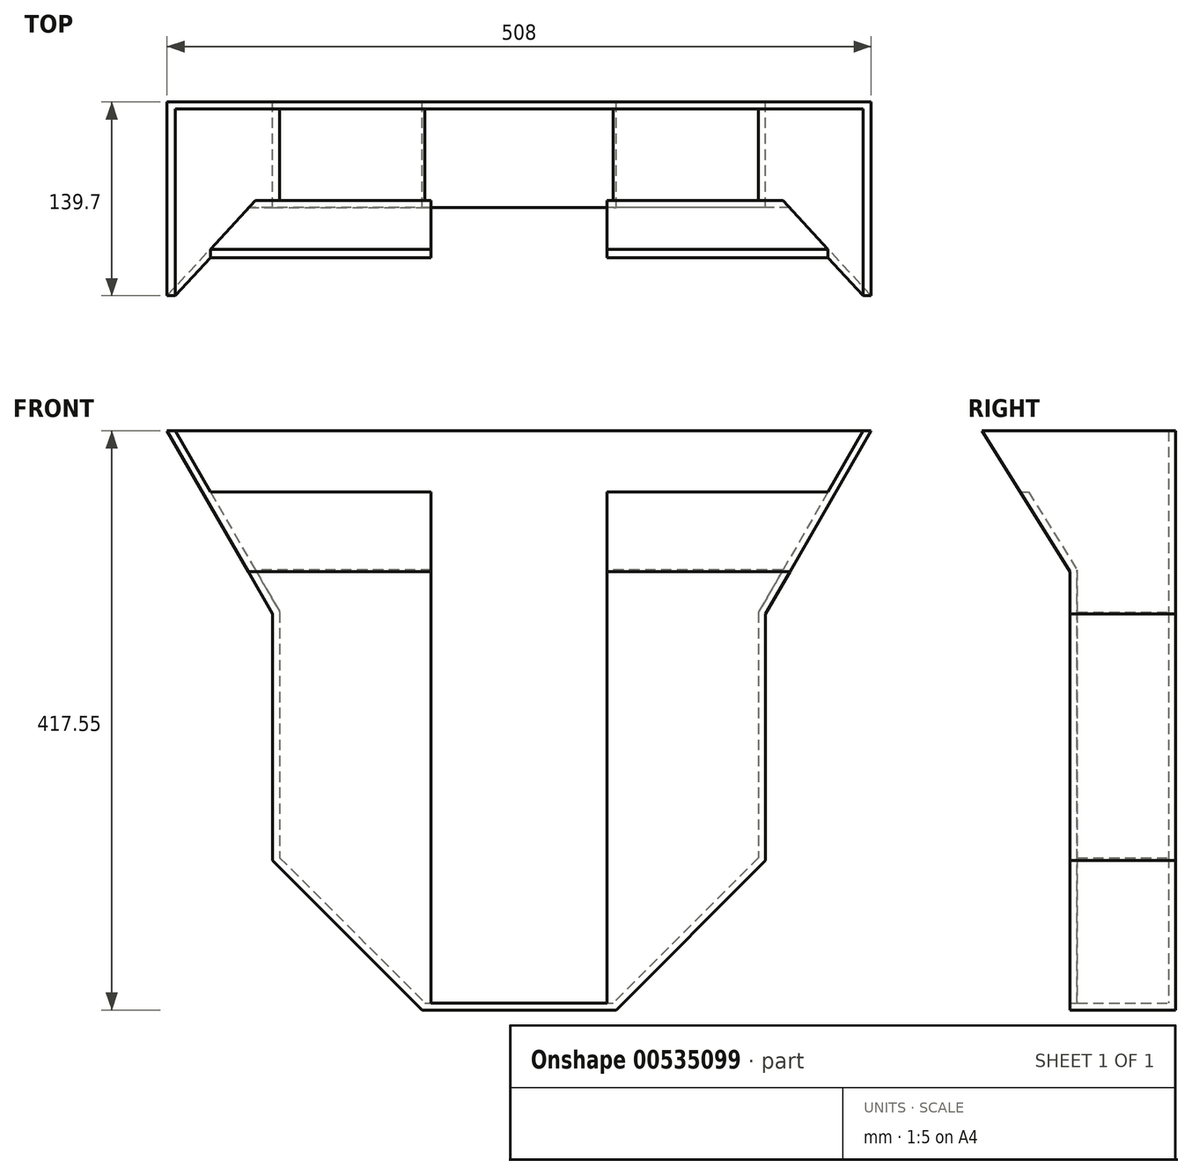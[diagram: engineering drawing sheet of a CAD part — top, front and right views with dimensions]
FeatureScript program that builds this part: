
annotation { "Feature Type Name" : "Feature", "Feature Type Description" : "" }
export const myFeature = defineFeature(function(context is Context, id is Id, definition is map)
    precondition{}
    {
        {
            var Q0;
            Q0=qCreatedBy(makeId("Front.planeOp"),FACE);
            var sketch = newSketch(context, id + "F0", { "sketchPlane" : qUnion([Q0])});
            skLineSegment(sketch, "E0", {"start": v(0, 0) * mm, "end": v(254, 0) * mm});
            skLineSegment(sketch, "E1", {"start": v(254, 0) * mm, "end": v(177.8, -131.98) * mm});
            skLineSegment(sketch, "E2", {"start": v(177.8, -131.98) * mm, "end": v(177.8, -309.78) * mm});
            skLineSegment(sketch, "E3", {"start": v(177.8, -309.78) * mm, "end": v(70.04, -417.55) * mm});
            skLineSegment(sketch, "E4", {"start": v(70.04, -417.55) * mm, "end": v(0, -417.55) * mm});
            skLineSegment(sketch, "E5.MirrorCS", {"start": v(0, 0) * mm, "end": v(-254, 0) * mm});
            skLineSegment(sketch, "E6.MirrorCS", {"start": v(-254, 0) * mm, "end": v(-177.8, -131.98) * mm});
            skLineSegment(sketch, "E7.MirrorCS", {"start": v(-177.8, -131.98) * mm, "end": v(-177.8, -309.78) * mm});
            skLineSegment(sketch, "E8.MirrorCS", {"start": v(-177.8, -309.78) * mm, "end": v(-70.04, -417.55) * mm});
            skLineSegment(sketch, "E9.MirrorCS", {"start": v(-70.04, -417.55) * mm, "end": v(0, -417.55) * mm});
            skSolve(sketch);
        }
        {
            var Q0;
            Q0=makeQuery(id+"F0.imprint","IMPRINT",FACE,{"disambiguationData":[TD([[makeQuery(id+"F0.imprint","IMPRINT",EDGE,{"derivedFrom":sQuery(id+"F0.wireOp",EDGE,"E0")}),-1.0]])]});
            extrude(context, id + "F1", {"entities" : qUnion([Q0]), "depth" : 76.2 * mm});
        }
        {
            var Q0;
            Q0=qCreatedBy(makeId("Right.planeOp"),FACE);
            var sketch = newSketch(context, id + "F2", { "sketchPlane" : qUnion([Q0])});
            skLineSegment(sketch, "E10", {"start": v(-76.2, 0) * mm, "end": v(-139.7, 0) * mm});
            skLineSegment(sketch, "E11", {"start": v(-139.7, 0) * mm, "end": v(-76.2, -101.6) * mm});
            skLineSegment(sketch, "E12", {"start": v(-76.2, -101.6) * mm, "end": v(-76.2, 0) * mm});
            skSolve(sketch);
        }
        {
            var Q0;
            Q0=qSketchRegion(id+"F2",true);
            var Q1;
            Q1=makeQuery(id+"F1.opExtrude","SWEPT_FACE",FACE,{"disambiguationData":[OSD([sQuery(id+"F0.wireOp",EDGE,"E1")])]});
            var Q2;
            Q2=makeQuery(id+"F1.opExtrude","SWEPT_FACE",FACE,{"disambiguationData":[OSD([sQuery(id+"F0.wireOp",EDGE,"E6.MirrorCS")])]});
            extrude(context, id + "F3", {"entities" : qUnion([Q0]), "operationType" : NewBodyOperationType.ADD, "endBound" : BoundingType.UP_TO_SURFACE, "endBoundEntityFace" : qUnion([Q1]), "depth" : 25.4 * mm, "hasSecondDirection" : true, "secondDirectionBound" : SecondDirectionBoundingType.UP_TO_SURFACE, "secondDirectionOppositeDirection" : true, "secondDirectionBoundEntityFace" : qUnion([Q2]), "secondDirectionDepth" : 25.4 * mm});
        }
        {
            var Q0;
            Q0=makeQuery(id+"F3.boolean.opBoolean","MERGE",FACE,{"derivedFrom":[makeQuery(id+"F1.opExtrude","SWEPT_FACE",FACE,{"disambiguationData":[OSD([sQuery(id+"F0.wireOp",EDGE,"E0"),sQuery(id+"F0.wireOp",EDGE,"E5.MirrorCS")])]}),makeQuery(id+"F3.opExtrude","SWEPT_FACE",FACE,{"disambiguationData":[OSD([sQuery(id+"F2.wireOp",EDGE,"E10")])]})]});
            shell(context, id + "F4", {"entities" : qUnion([Q0]), "thickness" : 5.08 * mm});
        }
        {
            var Q0;
            {var subQ0=sQuery(id+"F0.wireOp",EDGE,"E9.MirrorCS");var subQ1=sQuery(id+"F0.wireOp",EDGE,"E8.MirrorCS");var subQ2=sQuery(id+"F0.wireOp",EDGE,"E7.MirrorCS");var subQ3=sQuery(id+"F0.wireOp",EDGE,"E6.MirrorCS");var subQ4=sQuery(id+"F0.wireOp",EDGE,"E5.MirrorCS");var subQ5=sQuery(id+"F0.wireOp",EDGE,"E4");var subQ6=sQuery(id+"F0.wireOp",EDGE,"E3");var subQ7=sQuery(id+"F0.wireOp",EDGE,"E2");var subQ8=sQuery(id+"F0.wireOp",EDGE,"E1");var subQ9=sQuery(id+"F0.wireOp",EDGE,"E0");Q0=makeQuery(id+"F4.opShell","OFFSET_FACE",FACE,{"disambiguationData":[OSD([subQ9,subQ8,subQ7,subQ6,subQ5,subQ4,subQ3,subQ2,subQ1,subQ0]),TDD([makeQuery(id+"F1.opExtrude","CAP_FACE",FACE,{"disambiguationData":[OSD([subQ9,subQ8,subQ7,subQ6,subQ5,subQ4,subQ3,subQ2,subQ1,subQ0])],"isStart":true})])]});}
            var sketch = newSketch(context, id + "F5", { "sketchPlane" : qUnion([Q0])});
            skLineSegment(sketch, "E13.bottom", {"start": v(63.5, 0) * mm, "end": v(-63.5, 0) * mm});
            skLineSegment(sketch, "E13.top", {"start": v(63.5, -412.47) * mm, "end": v(-63.5, -412.47) * mm});
            skLineSegment(sketch, "E13.left", {"start": v(63.5, 0) * mm, "end": v(63.5, -412.47) * mm});
            skLineSegment(sketch, "E13.right", {"start": v(-63.5, 0) * mm, "end": v(-63.5, -412.47) * mm});
            skLineSegment(sketch, "E14", {"start": v(-248.13, 0) * mm, "end": v(-222.73, -44) * mm});
            skLineSegment(sketch, "E15", {"start": v(222.73, -44) * mm, "end": v(248.13, 0) * mm});
            skLineSegment(sketch, "E16", {"start": v(248.13, 0) * mm, "end": v(-248.13, 0) * mm});
            skLineSegment(sketch, "E17", {"start": v(-222.73, -44) * mm, "end": v(222.73, -44) * mm});
            skPoint(sketch, "E18.orphan", {"position": v(-210.43, -65.31) * mm});
            skPoint(sketch, "E19.orphan", {"position": v(210.43, -65.31) * mm});
            skSolve(sketch);
        }
        {
            var Q0;
            Q0=makeQuery(id+"F5.imprint","IMPRINT",FACE,{"disambiguationData":[TD([[makeQuery(id+"F5.imprint","IMPRINT",EDGE,{"derivedFrom":sQuery(id+"F5.wireOp",EDGE,"E13.bottom")}),-1.0]])]});
            var Q1;
            {var subQ0=sQuery(id+"F5.wireOp",EDGE,"E16");var subQ1=sQuery(id+"F5.wireOp",EDGE,"E13.left");var subQ2=makeQuery(id+"F5.imprint","INTERSECT",VERTEX,{"derivedFrom":[subQ1,subQ0]});Q1=makeQuery(id+"F5.imprint","IMPRINT",FACE,{"disambiguationData":[TD([[makeQuery(id+"F5.imprint","IMPRINT",EDGE,{"disambiguationData":[TD([[subQ2,-1.0]])],"derivedFrom":subQ1}),-1.0]])]});}
            var Q2;
            {var subQ5=sQuery(id+"F5.wireOp",EDGE,"E14");Q2=makeQuery(id+"F5.imprint","IMPRINT",FACE,{"disambiguationData":[TD([[makeQuery(id+"F5.imprint","IMPRINT",EDGE,{"derivedFrom":subQ5}),1.0]])]});}
            var Q3;
            {var subQ5=sQuery(id+"F5.wireOp",EDGE,"E15");Q3=makeQuery(id+"F5.imprint","IMPRINT",FACE,{"disambiguationData":[TD([[makeQuery(id+"F5.imprint","IMPRINT",EDGE,{"derivedFrom":subQ5}),-1.0]])]});}
            var Q4;
            Q4=makeQuery(id+"F1.opExtrude","CAP_FACE",FACE,{"disambiguationData":[OSD([sQuery(id+"F0.wireOp",EDGE,"E0"),sQuery(id+"F0.wireOp",EDGE,"E1"),sQuery(id+"F0.wireOp",EDGE,"E2"),sQuery(id+"F0.wireOp",EDGE,"E3"),sQuery(id+"F0.wireOp",EDGE,"E4"),sQuery(id+"F0.wireOp",EDGE,"E5.MirrorCS"),sQuery(id+"F0.wireOp",EDGE,"E6.MirrorCS"),sQuery(id+"F0.wireOp",EDGE,"E7.MirrorCS"),sQuery(id+"F0.wireOp",EDGE,"E8.MirrorCS"),sQuery(id+"F0.wireOp",EDGE,"E9.MirrorCS")])],"isStart":false});
            var Q5;
            {var subQ0=sQuery(id+"F5.wireOp",EDGE,"E13.top");Q5=makeQuery(id+"F5.imprint","IMPRINT",FACE,{"disambiguationData":[TD([[makeQuery(id+"F5.imprint","IMPRINT",EDGE,{"derivedFrom":subQ0}),1.0]])]});}
            extrude(context, id + "F6", {"entities" : qUnion([Q0, Q1, Q2, Q3, Q4, Q5]), "operationType" : NewBodyOperationType.REMOVE, "endBound" : BoundingType.THROUGH_ALL, "depth" : 25.4 * mm});
        }
    });
